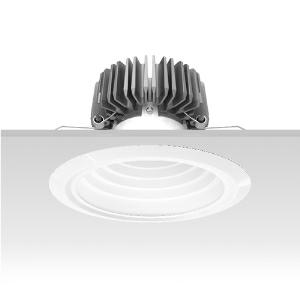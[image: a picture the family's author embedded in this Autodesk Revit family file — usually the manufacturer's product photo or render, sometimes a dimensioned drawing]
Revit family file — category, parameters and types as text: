
# Revit family: 3f_filippi_-_3f_reno_bianco_ampio_3f_filippi_-_30625_a01025_-_3f_reno_200_wh_2000-930_wide___vt_wh_226d
name_source: partatom
category: Lighting Fixtures
units: mm (PartAtom-declared; Revit-internal decimal feet)

## family parameters
Cut with Voids When Loaded = No
Host = Face
Light Source = No
Part Type = Normal
Room Calculation Point = No
Round Connector Dimension = Use Diameter
Shared = No

## types (1)
- 3F Filippi - 3F Reno Bianco Ampio (1 x LED, 1804 lm, 24 W, 3000 K)
    Apparent Load = 24 VA
    Approval mark = CE
    CIE Flux Codes = 75 94 99 100 100
    Color Rendering = 90
    Color Temperature = 3000 K
    Control Gear = Electronic ballast
    Default Elevation = 1800 mm
    Description = ILLUMINOTECHNICAL
Luminous efficiency 100% (DLOR 100%, ULOR 0%).
Initial luminous flux of the luminaire 1804 lm.
Direct symmetric wide distribution.
Installation Interdistance Transv.D = 1.56 x hu - Long.D = 1.56 x hu.
Average luminance <3000 cd/m² for radial angles >65°.
Tabular UGR (CIE 117 - 4H-8H; S=0.25H; 70/50/20): RUG 20.6 - 20.5.
Beam angle: 74° - 74°.
Luminous efficacy 75 lm/W.
Lifetime (L90/B10): 30000 h. (tq+25°C)
Lifetime (L85/B10): 50000 h. (tq+25°C)
Lifetime (L70/B10): 80000 h. (tq+25°C)
Sudden decreased luminous flux after 50000 hours: 0% (C0).
Photobiological safety in compliance with IEC/TR 62778: RG0 risk exempt, (IEC 62471).
In compliance with IEC/EN 62722-2-1 - IEC/EN 62717 standards.

SOURCE
Compact LED module 2000/930.
Energy efficiency class (UE 2019/2020 - UE 2019/2015): E.
CIE 13.3 Colour rendering index: CRI >90 (R9 >50%).
IES TM-30 Fidelity Index: Rf = 92 Rg = 101.
CCT nominal colour temperature 3000 K.
Colour initial tolerance (MacAdam): SDCM 3.
Zhaga Book 3 compliant.

MECHANICAL
Passive heat dissipator in die-casting aluminium, oversized, for optimum thermal management of the LED module.
Parabolic element with graduated/concentric rings in white polycarbonate.
Transparent external lens with glossy and satin differentiated surfaces, with a cooling and anti-insect system in methacrylate (PMMA).
Fastening spring clips in stainless steel.
Dimensions: diameter 226 mm, height 146 mm. Weight 1.07 kg.
IP44 protection degree for exposed part, IP20 for recessed part.
Mechanical strength to impacts IK06 (1 joule).
Glow-wire test resistance 650°C.

ELECTRICAL
Wiring on a separate unit.
Halogen Free electronic wiring 230V-50/60Hz, power factor 0.95, THD <25%, constant output current, SELV, class II, 1 driver.
Power of the luminaire 24 W.
ENEC - CE.
SAFE FLICKER: PstLM=<1 and SVM=<0.4 (IEC TR 61547-1 and IEC TR 63158), to ensure a more comfortable and safe light.
Luminaire compliant with EN 60598-2-22 for power supply from a centralised emergency system CPSS (Central Power Supply System), not incorporated in the luminaire - high risk areas excluded. The default power and flux are 100% in AC and 100% in DC.
Ambient temperature from 0°C to +25°C.
Temperature class T6 max 85°C.
Relative humidity UR: <85%.

INSTALLATION
Pull-up recessed fitting.
False ceiling carving: 200 mm.
All accessories dedicated to this product are available on the Catalog and on our website www.3F-Filippi.com.

ACCESSORIES
A01025 - VT transparent glass, tempered, not flammable, locked and in line with the trim, in white polycarbonate.

APPLICATIONS
Environments: architectural, commercial, exhibition areas, transit areas, corridors, shops, display windows, service areas.
In false ceilings with narrow voids.

WARNING
Luminaire designed for disposal/recycling at end-of-life.
Replaceable (LED only) light source by a professional. Replaceable control gear by a professional.
    Height = 0 mm  [stored 0 ft]
    Lamp = 1 x LED
    Lamp Light Flux = 1804 lm
    Lamp Power = 24 W
    Lamp count = 1
    Length = 226 mm
    Lifetime = 50000 h
    Luminous efficacy = 75 lm/W
    Manufacturer = 3F Filippi
    ModVariant = No
    Model = 3F Filippi - 30625+A01025 - 3F Reno 200 WH 2000-930 WIDE + VT WH
    Mounting Place = Ceiling
    Mounting Type = Recessed
    Number of Poles = 1
    OnlyDefault = Yes
    Power Factor = 1
    Product Name = 3F Filippi - 3F Reno Bianco Ampio
    Product group = recessed luminaire
    ProductGroupID = 4
    Protection Class = Protection class II
    Protection Degree = IP 20
    RLX_Detail_Level = 1
    RLX_Emergency_Light_Flux = 0 lm
    RLX_Emergency_Type = 0
    RLX_Emergency_Type_DB = No
    RlxData = <blob elided: 95645 chars, md5=c2d00fd8>
    Socket = socket
    Standby Power = 0 W
    System Light Flux = 1804 lm
    System Power = 24 W
    Type Comments = Product without accessories
    Type Image = 3ffilippi_3f_reno_200_wh__a01025.jpg
    URL = http://relux.com
    VarID = ---
    Voltage = 0 V
    Weight = 0.00 kg
    Width = 0 mm  [stored 0 ft]

note: [stored X ft] marks values corroborated as IEEE doubles in the binary element streams (Revit-internal decimal feet)

## geometry (parser evidence)
native form markers: Blend x4, Sweep x9
no freeform markers — native parametric forms only
